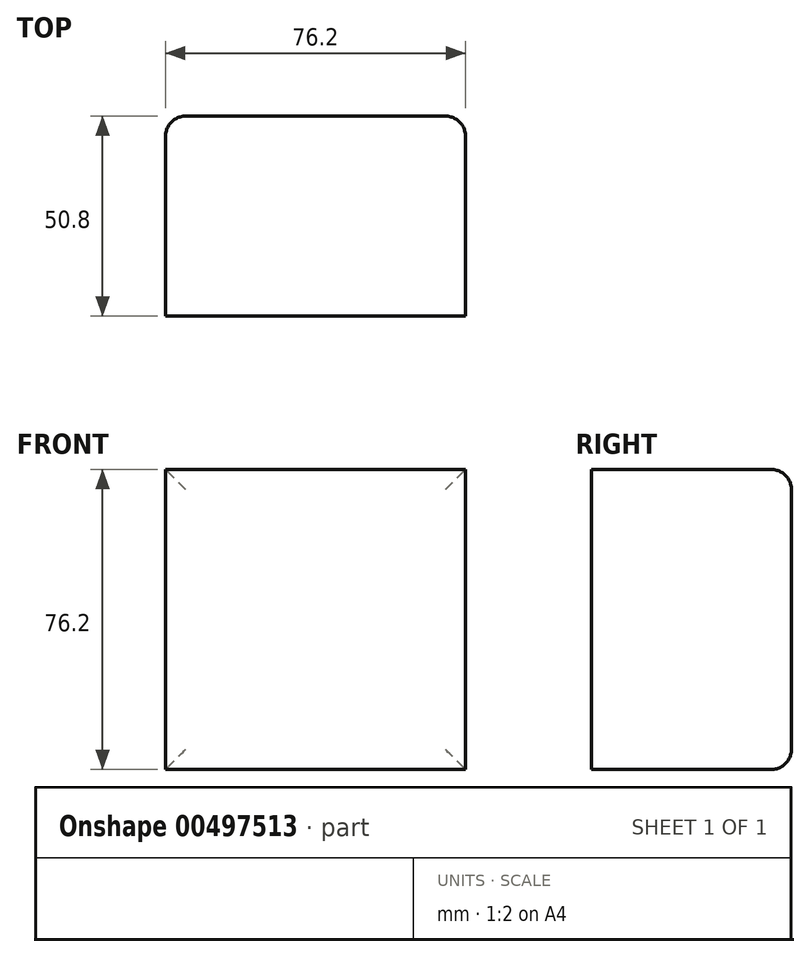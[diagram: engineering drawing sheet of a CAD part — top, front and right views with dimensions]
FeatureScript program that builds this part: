
annotation { "Feature Type Name" : "Feature", "Feature Type Description" : "" }
export const myFeature = defineFeature(function(context is Context, id is Id, definition is map)
    precondition{}
    {
        {
            var Q0;
            Q0=qCreatedBy(makeId("Top.planeOp"),FACE);
            var sketch = newSketch(context, id + "F0", { "sketchPlane" : qUnion([Q0])});
            skLineSegment(sketch, "E0.bottom", {"start": v(38.1, 25.4) * mm, "end": v(-38.1, 25.4) * mm});
            skLineSegment(sketch, "E0.top", {"start": v(38.1, -25.4) * mm, "end": v(-38.1, -25.4) * mm});
            skLineSegment(sketch, "E0.left", {"start": v(38.1, 25.4) * mm, "end": v(38.1, -25.4) * mm});
            skLineSegment(sketch, "E0.right", {"start": v(-38.1, 25.4) * mm, "end": v(-38.1, -25.4) * mm});
            skPoint(sketch, "E0.middle", {"position": v(0, 0) * mm});
            skSolve(sketch);
        }
        {
            var Q0;
            Q0=makeQuery(id+"F0.imprint","IMPRINT",FACE,{"disambiguationData":[TD([[makeQuery(id+"F0.imprint","IMPRINT",EDGE,{"derivedFrom":sQuery(id+"F0.wireOp",EDGE,"E0.bottom")}),1.0]])]});
            extrude(context, id + "F1", {"entities" : qUnion([Q0]), "depth" : 76.2 * mm});
        }
        {
            var Q0;
            Q0=makeQuery(id+"F1.opExtrude","SWEPT_FACE",FACE,{"disambiguationData":[OSD([sQuery(id+"F0.wireOp",EDGE,"E0.bottom")])]});
            fillet(context, id + "F2", {"entities" : qUnion([Q0]), "radius" : 5.08 * mm, "tangentPropagation" : true, "allowEdgeOverflow" : false});
        }
    });
